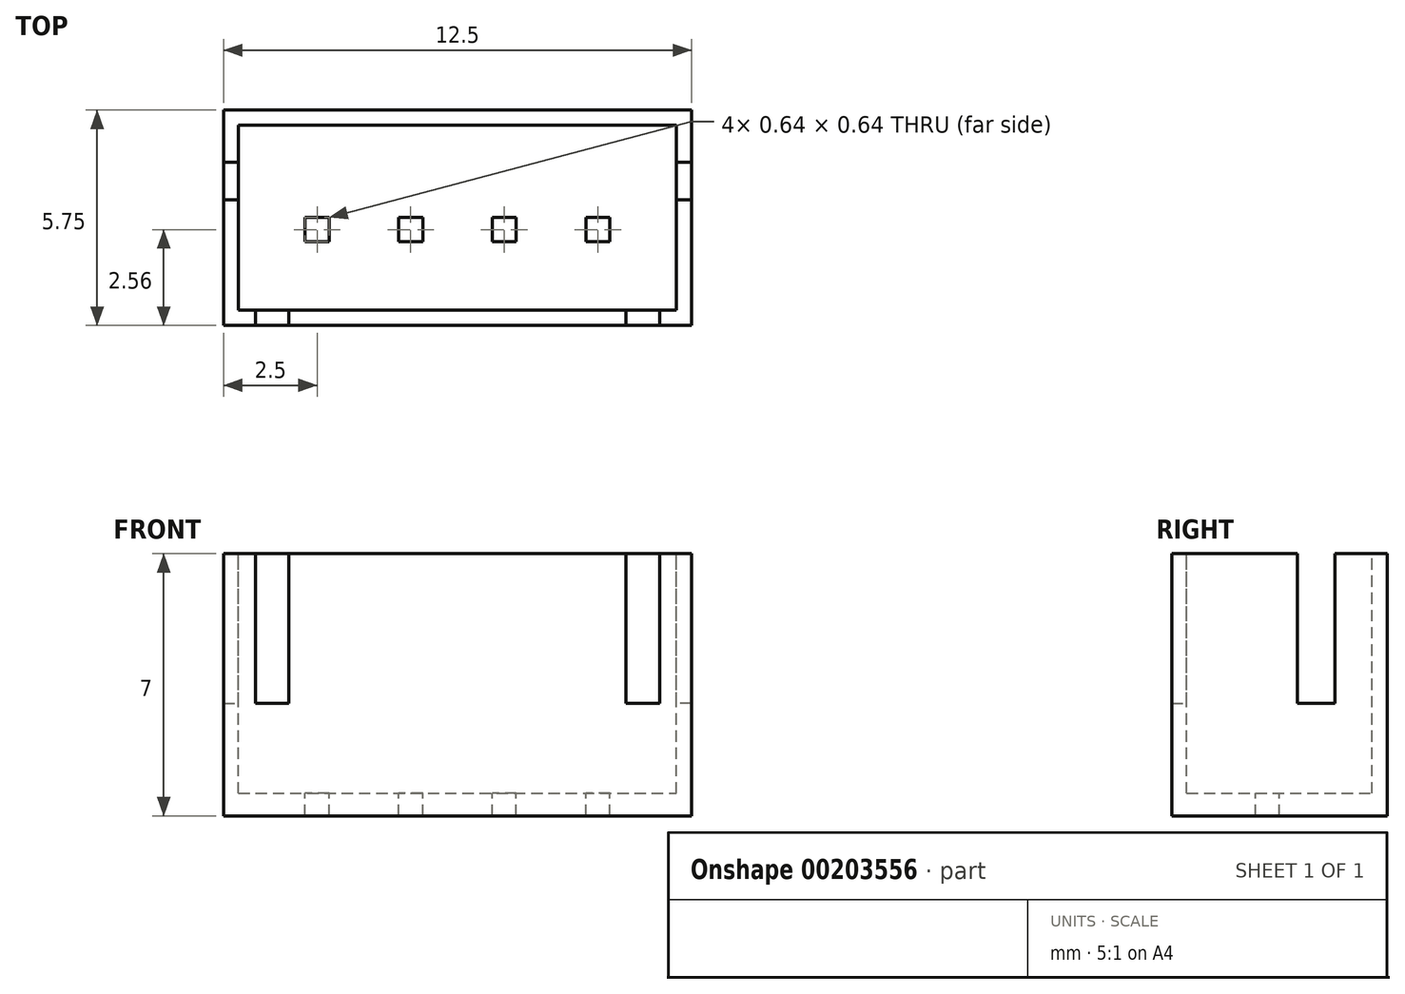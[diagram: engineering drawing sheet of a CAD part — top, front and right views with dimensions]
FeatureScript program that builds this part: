
annotation { "Feature Type Name" : "Feature", "Feature Type Description" : "" }
export const myFeature = defineFeature(function(context is Context, id is Id, definition is map)
    precondition{}
    {
        {
            assignVariable(context, id + "F0", {"name" : "w1", "anyValue" : 0.4});
        }
        {
            var Q0;
            Q0=qCreatedBy(makeId("Top.planeOp"),FACE);
            var sketch = newSketch(context, id + "F1", { "sketchPlane" : qUnion([Q0])});
            skLineSegment(sketch, "E0.bottom", {"start": v(6.25, -2.55) * mm, "end": v(-6.25, -2.56) * mm});
            skLineSegment(sketch, "E0.top", {"start": v(6.25, 3.2) * mm, "end": v(-6.25, 3.2) * mm});
            skLineSegment(sketch, "E0.left", {"start": v(6.25, -2.55) * mm, "end": v(6.25, 3.2) * mm});
            skLineSegment(sketch, "E0.right", {"start": v(-6.25, -2.56) * mm, "end": v(-6.25, 3.2) * mm});
            skPoint(sketch, "E0.middle", {"position": v(0, 0.32) * mm});
            skSolve(sketch);
        }
        {
            var Q0;
            Q0=makeQuery(id+"F1.imprint","IMPRINT",FACE,{"disambiguationData":[TD([[makeQuery(id+"F1.imprint","IMPRINT",EDGE,{"derivedFrom":sQuery(id+"F1.wireOp",EDGE,"E0.bottom")}),-1.0]])]});
            extrude(context, id + "F2", {"entities" : qUnion([Q0]), "depth" : 7 * mm});
        }
        {
            var Q0;
            Q0=makeQuery(id+"F2.opExtrude","CAP_FACE",FACE,{"disambiguationData":[OSD([sQuery(id+"F1.wireOp",EDGE,"E0.bottom"),sQuery(id+"F1.wireOp",EDGE,"E0.top"),sQuery(id+"F1.wireOp",EDGE,"E0.left"),sQuery(id+"F1.wireOp",EDGE,"E0.right")])],"isStart":false});
            var sketch = newSketch(context, id + "F3", { "sketchPlane" : qUnion([Q0])});
            skLineSegment(sketch, "E1.bottom", {"start": v(-5.85, -2.15) * mm, "end": v(5.85, -2.15) * mm});
            skLineSegment(sketch, "E1.top", {"start": v(-5.85, 2.8) * mm, "end": v(5.85, 2.8) * mm});
            skLineSegment(sketch, "E1.left", {"start": v(-5.85, -2.15) * mm, "end": v(-5.85, 2.8) * mm});
            skLineSegment(sketch, "E1.right", {"start": v(5.85, -2.15) * mm, "end": v(5.85, 2.8) * mm});
            skSolve(sketch);
        }
        {
            var Q0;
            Q0=makeQuery(id+"F3.imprint","IMPRINT",FACE,{"disambiguationData":[TD([[makeQuery(id+"F3.imprint","IMPRINT",EDGE,{"derivedFrom":sQuery(id+"F3.wireOp",EDGE,"E1.bottom")}),1.0]])]});
            extrude(context, id + "F4", {"entities" : qUnion([Q0]), "operationType" : NewBodyOperationType.REMOVE, "oppositeDirection" : true, "depth" : (7 - getVariable(context, 'w1') * 1.5) * mm});
        }
        {
            var Q0;
            Q0=makeQuery(id+"F4.boolean.opBoolean","COPY",FACE,{"derivedFrom":makeQuery(id+"F4.opExtrude","CAP_FACE",FACE,{"disambiguationData":[OSD([sQuery(id+"F3.wireOp",EDGE,"E1.bottom"),sQuery(id+"F3.wireOp",EDGE,"E1.top"),sQuery(id+"F3.wireOp",EDGE,"E1.left"),sQuery(id+"F3.wireOp",EDGE,"E1.right")])],"isStart":false})});
            var sketch = newSketch(context, id + "F5", { "sketchPlane" : qUnion([Q0])});
            skLineSegment(sketch, "E2", {"start": v(-5.85, 0.32) * mm, "end": v(5.85, 0.32) * mm, "construction": true});
            skLineSegment(sketch, "E3.bottom", {"start": v(-0.93, -0.32) * mm, "end": v(-1.57, -0.32) * mm});
            skLineSegment(sketch, "E3.top", {"start": v(-0.93, 0.32) * mm, "end": v(-1.57, 0.32) * mm});
            skLineSegment(sketch, "E3.left", {"start": v(-0.93, -0.32) * mm, "end": v(-0.93, 0.32) * mm});
            skLineSegment(sketch, "E3.right", {"start": v(-1.57, -0.32) * mm, "end": v(-1.57, 0.32) * mm});
            skPoint(sketch, "E3.middle", {"position": v(-1.25, 0) * mm});
            skLineSegment(sketch, "E4.1.0.0", {"start": v(1.57, 0.32) * mm, "end": v(0.93, 0.32) * mm});
            skLineSegment(sketch, "E4.1.0.1", {"start": v(1.57, -0.32) * mm, "end": v(0.93, -0.32) * mm});
            skLineSegment(sketch, "E4.1.0.2", {"start": v(1.57, -0.32) * mm, "end": v(1.57, 0.32) * mm});
            skPoint(sketch, "E4.1.0.3", {"position": v(1.25, 0) * mm});
            skLineSegment(sketch, "E4.1.0.4", {"start": v(0.93, -0.32) * mm, "end": v(0.93, 0.32) * mm});
            skLineSegment(sketch, "E4.2.0.0", {"start": v(4.07, 0.32) * mm, "end": v(3.43, 0.32) * mm});
            skLineSegment(sketch, "E4.2.0.1", {"start": v(4.07, -0.32) * mm, "end": v(3.43, -0.32) * mm});
            skLineSegment(sketch, "E4.2.0.2", {"start": v(4.07, -0.32) * mm, "end": v(4.07, 0.32) * mm});
            skPoint(sketch, "E4.2.0.3", {"position": v(3.75, 0) * mm});
            skLineSegment(sketch, "E4.2.0.4", {"start": v(3.43, -0.32) * mm, "end": v(3.43, 0.32) * mm});
            skLineSegment(sketch, "E4.direction1", {"start": v(-1.57, -0.32) * mm, "end": v(0.93, -0.32) * mm, "construction": true});
            skLineSegment(sketch, "E5.1.0.0", {"start": v(-3.43, -0.32) * mm, "end": v(-4.07, -0.32) * mm});
            skPoint(sketch, "E5.1.0.1", {"position": v(-3.75, 0) * mm});
            skLineSegment(sketch, "E5.1.0.2", {"start": v(-3.43, 0.32) * mm, "end": v(-4.07, 0.32) * mm});
            skLineSegment(sketch, "E5.1.0.3", {"start": v(-3.43, -0.32) * mm, "end": v(-3.43, 0.32) * mm});
            skLineSegment(sketch, "E5.1.0.4", {"start": v(-4.07, -0.32) * mm, "end": v(-4.07, 0.32) * mm});
            skLineSegment(sketch, "E5.direction1", {"start": v(-1.57, -0.32) * mm, "end": v(-4.07, -0.32) * mm, "construction": true});
            skSolve(sketch);
        }
        {
            var Q0;
            Q0=makeQuery(id+"F5.imprint","IMPRINT",FACE,{"disambiguationData":[TD([[makeQuery(id+"F5.imprint","IMPRINT",EDGE,{"derivedFrom":sQuery(id+"F5.wireOp",EDGE,"E3.bottom")}),-1.0]])]});
            var Q1;
            Q1=makeQuery(id+"F5.imprint","IMPRINT",FACE,{"disambiguationData":[TD([[makeQuery(id+"F5.imprint","IMPRINT",EDGE,{"derivedFrom":sQuery(id+"F5.wireOp",EDGE,"E5.1.0.0")}),-1.0]])]});
            var Q2;
            Q2=makeQuery(id+"F5.imprint","IMPRINT",FACE,{"disambiguationData":[TD([[makeQuery(id+"F5.imprint","IMPRINT",EDGE,{"derivedFrom":sQuery(id+"F5.wireOp",EDGE,"E5.2.0.0")}),-1.0]])]});
            var Q3;
            Q3=makeQuery(id+"F5.imprint","IMPRINT",FACE,{"disambiguationData":[TD([[makeQuery(id+"F5.imprint","IMPRINT",EDGE,{"derivedFrom":sQuery(id+"F5.wireOp",EDGE,"E4.1.0.0")}),1.0]])]});
            var Q4;
            Q4=makeQuery(id+"F5.imprint","IMPRINT",FACE,{"disambiguationData":[TD([[makeQuery(id+"F5.imprint","IMPRINT",EDGE,{"derivedFrom":sQuery(id+"F5.wireOp",EDGE,"E4.2.0.0")}),1.0]])]});
            extrude(context, id + "F6", {"entities" : qUnion([Q0, Q1, Q2, Q3, Q4]), "operationType" : NewBodyOperationType.REMOVE, "endBound" : BoundingType.THROUGH_ALL, "oppositeDirection" : true, "depth" : 25 * mm});
        }
        {
            var Q0;
            Q0=makeQuery(id+"F2.opExtrude","CAP_FACE",FACE,{"disambiguationData":[OSD([sQuery(id+"F1.wireOp",EDGE,"E0.bottom"),sQuery(id+"F1.wireOp",EDGE,"E0.top"),sQuery(id+"F1.wireOp",EDGE,"E0.left"),sQuery(id+"F1.wireOp",EDGE,"E0.right")])],"isStart":false});
            var sketch = newSketch(context, id + "F7", { "sketchPlane" : qUnion([Q0])});
            skLineSegment(sketch, "E6.bottom", {"start": v(-5.4, -2.56) * mm, "end": v(-4.5, -2.56) * mm});
            skLineSegment(sketch, "E6.top", {"start": v(-5.4, -2.15) * mm, "end": v(-4.5, -2.15) * mm});
            skLineSegment(sketch, "E6.left", {"start": v(-5.4, -2.56) * mm, "end": v(-5.4, -2.15) * mm});
            skLineSegment(sketch, "E6.right", {"start": v(-4.5, -2.56) * mm, "end": v(-4.5, -2.15) * mm});
            skLineSegment(sketch, "E7", {"start": v(0, 2.12) * mm, "end": v(0, -2.55) * mm, "construction": true});
            skPoint(sketch, "E7.startSnap0", {"position": v(0, 2.8) * mm});
            skLineSegment(sketch, "E8.MirrorCS", {"start": v(5.4, -2.15) * mm, "end": v(4.5, -2.15) * mm});
            skLineSegment(sketch, "E9.MirrorCS", {"start": v(5.4, -2.56) * mm, "end": v(4.5, -2.56) * mm});
            skLineSegment(sketch, "E10.MirrorCS", {"start": v(5.4, -2.56) * mm, "end": v(5.4, -2.15) * mm});
            skLineSegment(sketch, "E11.MirrorCS", {"start": v(4.5, -2.55) * mm, "end": v(4.5, -2.15) * mm});
            skSolve(sketch);
        }
        {
            var Q0;
            Q0=makeQuery(id+"F7.imprint","IMPRINT",FACE,{"disambiguationData":[TD([[makeQuery(id+"F7.imprint","IMPRINT",EDGE,{"derivedFrom":sQuery(id+"F7.wireOp",EDGE,"E6.bottom")}),-1.0]])]});
            var Q1;
            Q1=makeQuery(id+"F7.imprint","IMPRINT",FACE,{"disambiguationData":[TD([[makeQuery(id+"F7.imprint","IMPRINT",EDGE,{"derivedFrom":sQuery(id+"F7.wireOp",EDGE,"E8.MirrorCS")}),-1.0]])]});
            extrude(context, id + "F8", {"entities" : qUnion([Q0, Q1]), "operationType" : NewBodyOperationType.REMOVE, "oppositeDirection" : true, "depth" : 4 * mm});
        }
        {
            var Q0;
            {var subQ0=sQuery(id+"F1.wireOp",EDGE,"E0.right");var subQ1=sQuery(id+"F1.wireOp",EDGE,"E0.left");var subQ2=sQuery(id+"F1.wireOp",EDGE,"E0.top");var subQ3=sQuery(id+"F1.wireOp",EDGE,"E0.bottom");Q0=makeQuery(id+"F8.boolean.opBoolean","SPLIT",FACE,{"disambiguationData":[TD([makeQuery(id+"F2.opExtrude","SWEPT_FACE",FACE,{"disambiguationData":[OSD([subQ2])]})])],"derivedFrom":makeQuery(id+"F2.opExtrude","CAP_FACE",FACE,{"disambiguationData":[OSD([subQ3,subQ2,subQ1,subQ0])],"isStart":false})});}
            var sketch = newSketch(context, id + "F9", { "sketchPlane" : qUnion([Q0])});
            skLineSegment(sketch, "E12.bottom", {"start": v(-6.25, 1.8) * mm, "end": v(-5.85, 1.8) * mm});
            skLineSegment(sketch, "E12.top", {"start": v(-6.25, 0.8) * mm, "end": v(-5.85, 0.8) * mm});
            skLineSegment(sketch, "E12.left", {"start": v(-6.25, 1.8) * mm, "end": v(-6.25, 0.8) * mm});
            skLineSegment(sketch, "E12.right", {"start": v(-5.85, 1.8) * mm, "end": v(-5.85, 0.8) * mm});
            skLineSegment(sketch, "E13", {"start": v(0, 2.8) * mm, "end": v(0, -2.9) * mm, "construction": true});
            skLineSegment(sketch, "E14.MirrorCS", {"start": v(6.25, 1.8) * mm, "end": v(6.25, 0.8) * mm});
            skLineSegment(sketch, "E15.MirrorCS", {"start": v(6.25, 1.8) * mm, "end": v(5.85, 1.8) * mm});
            skLineSegment(sketch, "E16.MirrorCS", {"start": v(6.25, 0.8) * mm, "end": v(5.85, 0.8) * mm});
            skLineSegment(sketch, "E17.MirrorCS", {"start": v(5.85, 1.8) * mm, "end": v(5.85, 0.8) * mm});
            skSolve(sketch);
        }
        {
            var Q0;
            Q0=makeQuery(id+"F9.imprint","IMPRINT",FACE,{"disambiguationData":[TD([[makeQuery(id+"F9.imprint","IMPRINT",EDGE,{"derivedFrom":sQuery(id+"F9.wireOp",EDGE,"E12.bottom")}),-1.0]])]});
            var Q1;
            Q1=makeQuery(id+"F9.imprint","IMPRINT",FACE,{"disambiguationData":[TD([[makeQuery(id+"F9.imprint","IMPRINT",EDGE,{"derivedFrom":sQuery(id+"F9.wireOp",EDGE,"E14.MirrorCS")}),1.0]])]});
            extrude(context, id + "F10", {"entities" : qUnion([Q0, Q1]), "operationType" : NewBodyOperationType.REMOVE, "oppositeDirection" : true, "depth" : 4 * mm});
        }
    });
